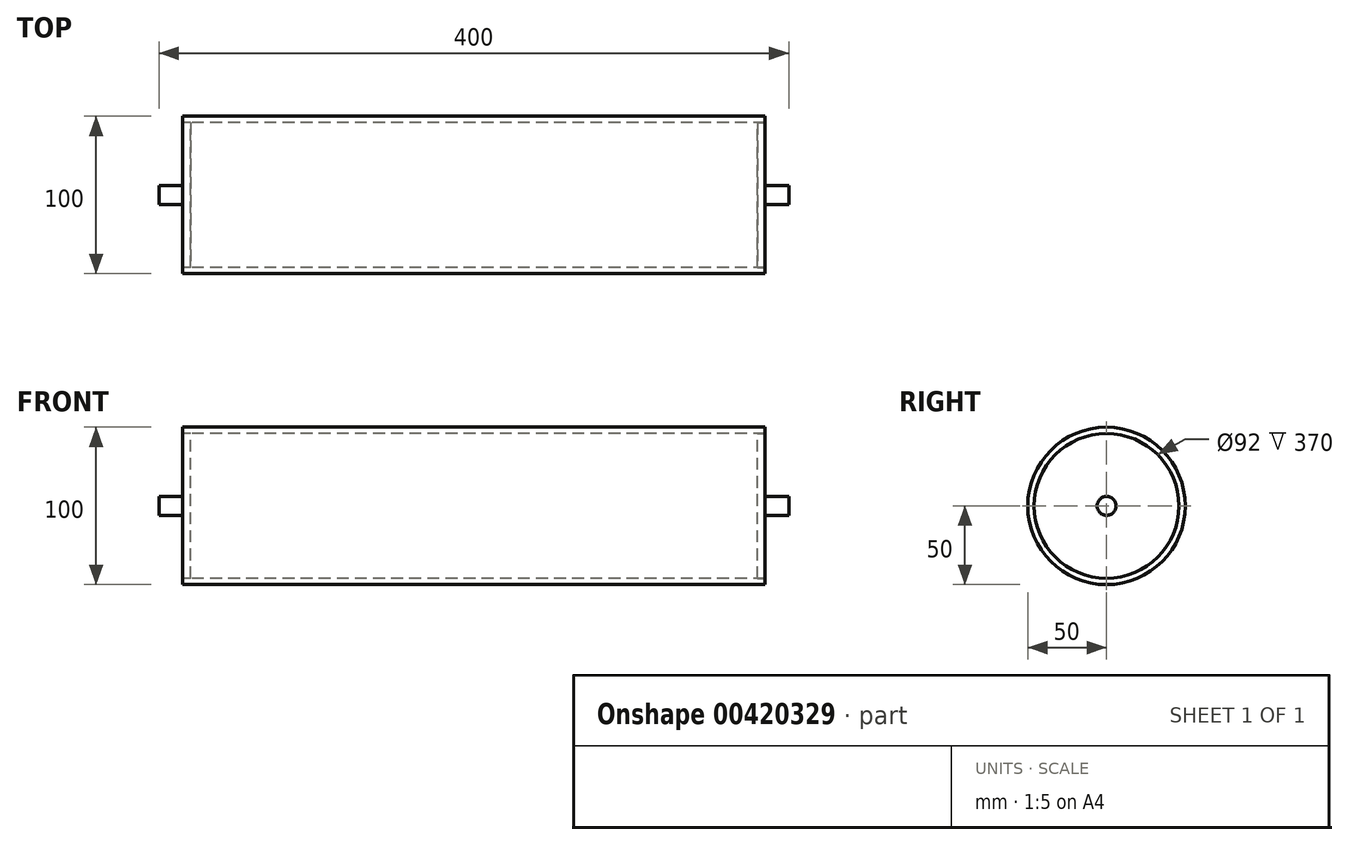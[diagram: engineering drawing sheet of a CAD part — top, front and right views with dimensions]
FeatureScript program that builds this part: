
annotation { "Feature Type Name" : "Feature", "Feature Type Description" : "" }
export const myFeature = defineFeature(function(context is Context, id is Id, definition is map)
    precondition{}
    {
        {
            var Q0;
            Q0=qCreatedBy(makeId("Right.planeOp"),FACE);
            var sketch = newSketch(context, id + "F0", { "sketchPlane" : qUnion([Q0])});
            skCircle(sketch, "E0", {"center": v(0, 0) * mm, "radius": 46 * mm});
            skCircle(sketch, "E1", {"center": v(0, 0) * mm, "radius": 50 * mm});
            skSolve(sketch);
        }
        {
            var Q0;
            Q0=qSketchRegion(id+"F0",true);
            extrude(context, id + "F1", {"entities" : qUnion([Q0]), "depth" : 370 * mm});
        }
        {
            var Q0;
            Q0=makeQuery(id+"F1.opExtrude","CAP_FACE",FACE,{"disambiguationData":[OSD([sQuery(id+"F0.wireOp",EDGE,"E0"),sQuery(id+"F0.wireOp",EDGE,"E1")])],"isStart":true});
            var sketch = newSketch(context, id + "F2", { "sketchPlane" : qUnion([Q0])});
            skCircle(sketch, "E2", {"center": v(0, 0) * mm, "radius": 46 * mm});
            skSolve(sketch);
        }
        {
            var Q0;
            Q0=qSketchRegion(id+"F2",true);
            extrude(context, id + "F3", {"entities" : qUnion([Q0]), "oppositeDirection" : true, "depth" : 5 * mm});
        }
        {
            var Q0;
            Q0=makeQuery(id+"F3.opExtrude","CAP_FACE",FACE,{"disambiguationData":[OSD([sQuery(id+"F2.wireOp",EDGE,"E2")])],"isStart":true});
            var sketch = newSketch(context, id + "F4", { "sketchPlane" : qUnion([Q0])});
            skCircle(sketch, "E3", {"center": v(0, 0) * mm, "radius": 6 * mm});
            skSolve(sketch);
        }
        {
            var Q0;
            Q0=qSketchRegion(id+"F4",true);
            extrude(context, id + "F5", {"entities" : qUnion([Q0]), "operationType" : NewBodyOperationType.ADD, "depth" : 15 * mm});
        }
        {
            var Q0;
            Q0=makeQuery(id+"F1.opExtrude","CAP_FACE",FACE,{"disambiguationData":[OSD([sQuery(id+"F0.wireOp",EDGE,"E0"),sQuery(id+"F0.wireOp",EDGE,"E1")])],"isStart":false});
            var sketch = newSketch(context, id + "F6", { "sketchPlane" : qUnion([Q0])});
            skCircle(sketch, "E4", {"center": v(0, 0) * mm, "radius": 46 * mm});
            skSolve(sketch);
        }
        {
            var Q0;
            Q0=qSketchRegion(id+"F6",true);
            extrude(context, id + "F7", {"entities" : qUnion([Q0]), "oppositeDirection" : true, "depth" : 5 * mm});
        }
        {
            var Q0;
            Q0=makeQuery(id+"F7.opExtrude","CAP_FACE",FACE,{"disambiguationData":[OSD([sQuery(id+"F6.wireOp",EDGE,"E4")])],"isStart":true});
            var sketch = newSketch(context, id + "F8", { "sketchPlane" : qUnion([Q0])});
            skCircle(sketch, "E5", {"center": v(0, 0) * mm, "radius": 6 * mm});
            skSolve(sketch);
        }
        {
            var Q0;
            Q0=qSketchRegion(id+"F8",true);
            extrude(context, id + "F9", {"entities" : qUnion([Q0]), "operationType" : NewBodyOperationType.ADD, "depth" : 15 * mm});
        }
    });
